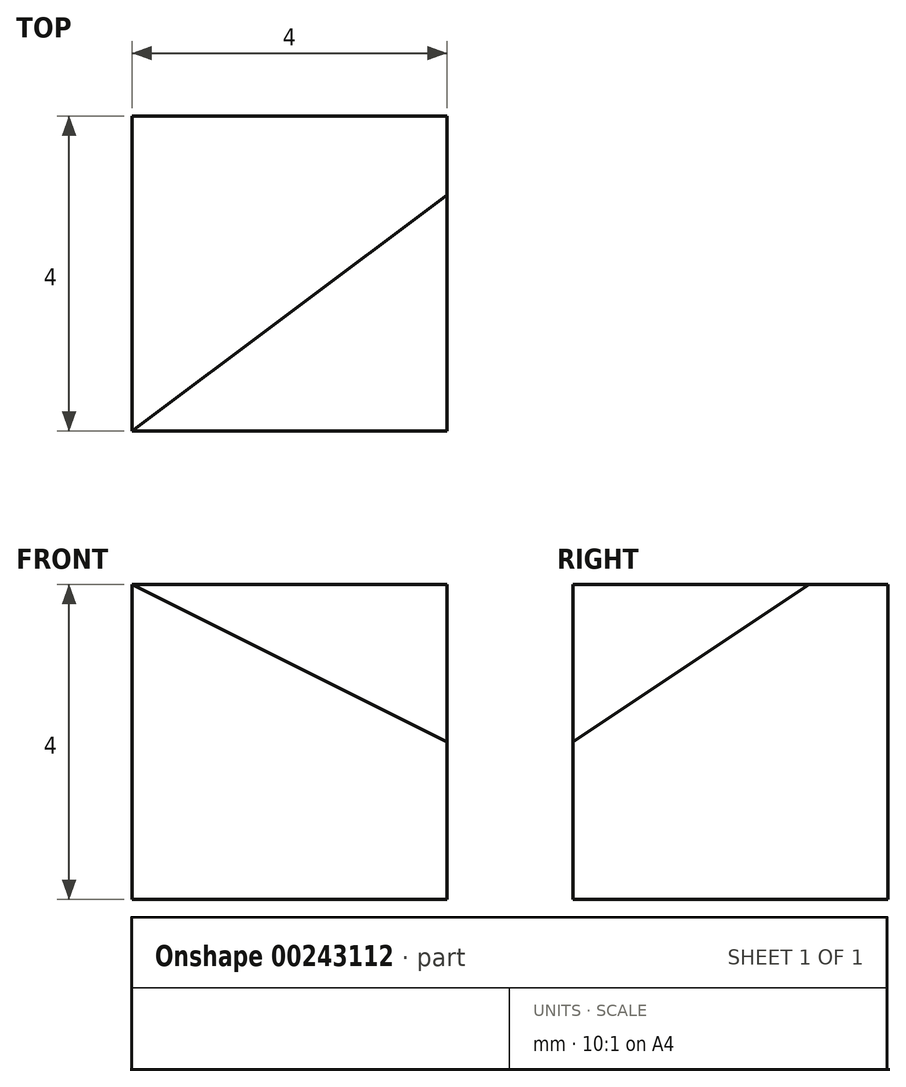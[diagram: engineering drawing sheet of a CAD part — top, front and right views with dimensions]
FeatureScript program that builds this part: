
annotation { "Feature Type Name" : "Feature", "Feature Type Description" : "" }
export const myFeature = defineFeature(function(context is Context, id is Id, definition is map)
    precondition{}
    {
        {
            var Q0;
            Q0=qCreatedBy(makeId("Front.planeOp"),FACE);
            var sketch = newSketch(context, id + "F0", { "sketchPlane" : qUnion([Q0])});
            skLineSegment(sketch, "E0", {"start": v(0, 0) * mm, "end": v(4, 0) * mm});
            skLineSegment(sketch, "E1", {"start": v(4, 0) * mm, "end": v(4, 4) * mm});
            skLineSegment(sketch, "E2", {"start": v(4, 4) * mm, "end": v(0, 4) * mm});
            skLineSegment(sketch, "E3", {"start": v(0, 4) * mm, "end": v(0, 0) * mm});
            skSolve(sketch);
        }
        {
            var Q0;
            Q0=makeQuery(id+"F0.imprint","IMPRINT",FACE,{"disambiguationData":[TD([[makeQuery(id+"F0.imprint","IMPRINT",EDGE,{"derivedFrom":sQuery(id+"F0.wireOp",EDGE,"E0")}),1.0]])]});
            extrude(context, id + "F1", {"entities" : qUnion([Q0]), "depth" : 4 * mm});
        }
        {
            var Q0;
            Q0=makeQuery(id+"F1.opExtrude","CAP_FACE",FACE,{"disambiguationData":[OSD([sQuery(id+"F0.wireOp",EDGE,"E0"),sQuery(id+"F0.wireOp",EDGE,"E1"),sQuery(id+"F0.wireOp",EDGE,"E2"),sQuery(id+"F0.wireOp",EDGE,"E3")])],"isStart":false});
            var sketch = newSketch(context, id + "F2", { "sketchPlane" : qUnion([Q0])});
            skLineSegment(sketch, "E4", {"start": v(4, 0) * mm, "end": v(4, 2) * mm});
            skLineSegment(sketch, "E5", {"start": v(4, 2) * mm, "end": v(0, 4) * mm});
            skSolve(sketch);
        }
        {
            var Q0;
            Q0=makeQuery(id+"F1.opExtrude","SWEPT_FACE",FACE,{"disambiguationData":[OSD([sQuery(id+"F0.wireOp",EDGE,"E2")])]});
            var sketch = newSketch(context, id + "F3", { "sketchPlane" : qUnion([Q0])});
            skLineSegment(sketch, "E6", {"start": v(4, -1) * mm, "end": v(0, -4) * mm});
            skLineSegment(sketch, "E7", {"start": v(4, -1) * mm, "end": v(4, 0) * mm});
            skSolve(sketch);
        }
        {
            var Q0;
            Q0=sQuery(id+"F3.wireOp",VERTEX,"E7.start");
            var Q1;
            Q1=sQuery(id+"F2.wireOp",VERTEX,"E5.end");
            var Q2;
            Q2=sQuery(id+"F2.wireOp",VERTEX,"E5.start");
            cPlane(context, id + "F4", {"entities" : qUnion([Q0, Q1, Q2]), "cplaneType" : CPlaneType.THREE_POINT, "offset" : 25 * mm, "width" : 150 * mm, "height" : 150 * mm});
        }
        {
            var Q0;
            Q0=qCreatedBy(id+"F4.planeOp",FACE);
            var sketch = newSketch(context, id + "F5", { "sketchPlane" : qUnion([Q0])});
            skPoint(sketch, "E8.0", {"position": v(-2.13, 1.1) * mm});
            skPoint(sketch, "E8.1", {"position": v(2.2, 2.22) * mm});
            skPoint(sketch, "E8.2", {"position": v(2.2, -1.39) * mm});
            skLineSegment(sketch, "E9", {"start": v(2.2, -1.39) * mm, "end": v(-2.13, 1.1) * mm});
            skLineSegment(sketch, "E10", {"start": v(-2.13, 1.1) * mm, "end": v(2.2, 2.22) * mm});
            skLineSegment(sketch, "E11", {"start": v(2.2, 2.22) * mm, "end": v(2.2, -1.39) * mm});
            skSolve(sketch);
        }
        {
            var Q0;
            Q0 = qSketchRegion(id + "F5", true);
            extrude(context, id + "F6", {"entities" : qUnion([Q0]), "operationType" : NewBodyOperationType.REMOVE, "oppositeDirection" : true, "depth" : 25 * mm});
        }
    });
